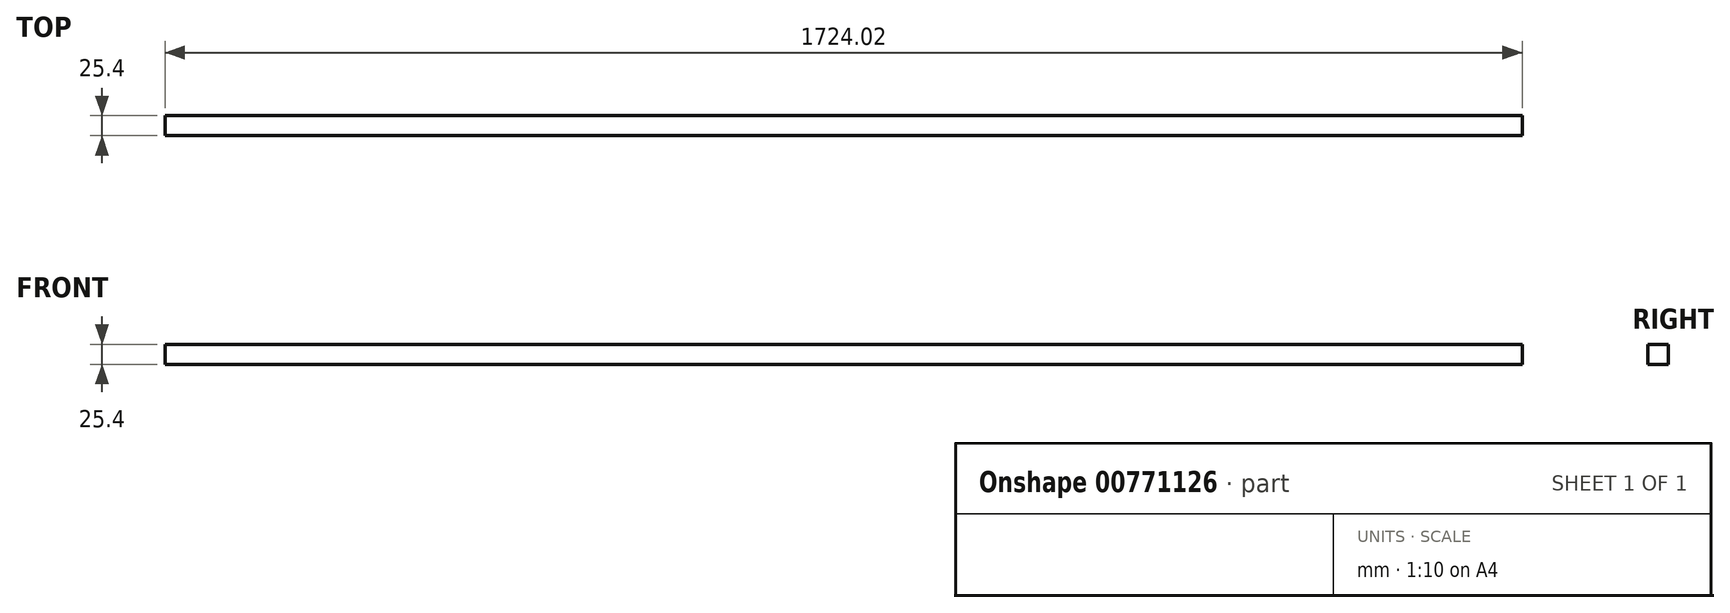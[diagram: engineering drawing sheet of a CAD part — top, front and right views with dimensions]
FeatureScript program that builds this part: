
annotation { "Feature Type Name" : "Feature", "Feature Type Description" : "" }
export const myFeature = defineFeature(function(context is Context, id is Id, definition is map)
    precondition{}
    {
        {
            var Q0;
            Q0=qCreatedBy(makeId("Right.planeOp"),FACE);
            var sketch = newSketch(context, id + "F0", { "sketchPlane" : qUnion([Q0])});
            skLineSegment(sketch, "E0.bottom", {"start": v(-12.7, 12.7) * mm, "end": v(12.7, 12.7) * mm});
            skLineSegment(sketch, "E0.top", {"start": v(-12.7, -12.7) * mm, "end": v(12.7, -12.7) * mm});
            skLineSegment(sketch, "E0.left", {"start": v(-12.7, 12.7) * mm, "end": v(-12.7, -12.7) * mm});
            skLineSegment(sketch, "E0.right", {"start": v(12.7, 12.7) * mm, "end": v(12.7, -12.7) * mm});
            skPoint(sketch, "E0.middle", {"position": v(0, 0) * mm});
            skSolve(sketch);
        }
        {
            var Q0;
            Q0 = qSketchRegion(id + "F0", true);
            extrude(context, id + "F1", {"entities" : qUnion([Q0]), "endBound" : BoundingType.SYMMETRIC, "depth" : 1724.02 * mm, "offsetDistance" : 25.4 * mm});
        }
    });
